# Revit family: Ворота ВПО-60
name_source: partatom
category: Двери
revit_build: Autodesk Revit 2017 (Build: 20160225_1515(x64)
units: mm (PartAtom-declared; Revit-internal decimal feet)

## family parameters
Всегда вертикально = Да
Заголовок OmniClass = Doors
Номер OmniClass = 23.30.10.00
Общий = Нет
Основа = Стена
При загрузке вырезать с полостями = Нет
Точка расчета площади = Нет

## types (10) — shared parameters
ADSK_URL страницы изделия = http://dwrcenter.ru
ADSK_Завод-изготовитель = ДВР Центр, г.Москва
ADSK_Наименование = ВПО-ОГНЕДЕКОР-60К
ADSK_Наименование краткое = ВПО-60
ADSK_Обозначение = ГОСТ 31174-2003, ГОСТ 53307-2009
ADSK_Предел огнестойкости = EI-60
URL = http://dwrcenter.ru
Группа модели = Ворота
Замыкание стены = По основе
Изготовитель = ДВР Центр, г.Москва, +7-495-4-112-911
Материал коробки = <По категории>
Материал створки = <По категории>
Огнестойкость = EI-60
Описание = Ворота противопожарные откатные
Телефоны изготовителя = +7-495-4-112-911, +7-495-5-103-206
Тип конструкций = Ворота противопожарные откатные, ГОСТ 53307-2009
Толщина = 260 мм
Функция = Внутренние слои
zero-valued in all types: ADSK_Количество, ADSK_Откосы_Глубина, ADSK_Толщина стены, ADSK_Толщина стены (отчет)

## per-type parameters (varying)
| type | ADSK_Открывание | Вылет на плане | Высота | До привода | Левое исполнение | Правое исполнение | Привод | Противовес | Сдвиг балки влево | Сдвиг балки вправо | Смещение противовеса | Смещение ручки | Ширина | Ширина секции | Ширина створки | Электромеханический привод |
| ВПО-ОГНЕДЕКОР-60Кп, проем 3000х3000 | Правое исполнение | 1248 мм | 3000 мм | 2820 мм | Нет | Да | Алюминий | Нет | 0 мм | 3120 мм | 3340 мм | 2902 мм | 3000 мм | 624 мм | 3120 мм | Нет |
| ВПО-ОГНЕДЕКОР-60Кл, проем 3000х3000 | Левое исполнение | 1248 мм | 3000 мм | 100 мм | Да | Нет | <По категории> | Да | 3120 мм | 0 мм | 0 мм | 109 мм | 3000 мм | 624 мм | 3120 мм | Да |
| ВПО-ОГНЕДЕКОР-60Кп, проем 3000х2500 | Правое исполнение | 1248 мм | 2500 мм | 2820 мм | Нет | Да | <По категории> | Да | 0 мм | 3120 мм | 3340 мм | 2902 мм | 3000 мм | 624 мм | 3120 мм | Да |
| ВПО-ОГНЕДЕКОР-60Кл, проем 3000х2500 | Левое исполнение | 1248 мм | 2500 мм | 100 мм | Да | Нет | <По категории> | Да | 3120 мм | 0 мм | 0 мм | 109 мм | 3000 мм | 624 мм | 3120 мм | Да |
| ВПО-ОГНЕДЕКОР-60Кп, проем 3500х2500 | Правое исполнение | 1448 мм | 2500 мм | 3320 мм | Нет | Да | <По категории> | Да | 0 мм | 3620 мм | 3840 мм | 3402 мм | 3500 мм | 724 мм | 3620 мм | Да |
| ВПО-ОГНЕДЕКОР-60Кл, проем 3500х2500 | Левое исполнение | 1448 мм | 2500 мм | 100 мм | Да | Нет | <По категории> | Да | 3620 мм | 0 мм | 0 мм | 109 мм | 3500 мм | 724 мм | 3620 мм | Да |
| ВПО-ОГНЕДЕКОР-60Кп, проем 3500х3000 | Правое исполнение | 1448 мм | 3000 мм | 3320 мм | Нет | Да | <По категории> | Да | 0 мм | 3620 мм | 3840 мм | 3402 мм | 3500 мм | 724 мм | 3620 мм | Да |
| ВПО-ОГНЕДЕКОР-60Кл, проем 3500х3000 | Левое исполнение | 1448 мм | 3000 мм | 100 мм | Да | Нет | <По категории> | Да | 3620 мм | 0 мм | 0 мм | 109 мм | 3500 мм | 724 мм | 3620 мм | Да |
| ВПО-ОГНЕДЕКОР-60Кп, проем 2500х2500 | Правое исполнение | 1048 мм | 2500 мм | 2320 мм | Нет | Да | <По категории> | Да | 0 мм | 2620 мм | 2840 мм | 2402 мм | 2500 мм | 524 мм | 2620 мм | Да |
| ВПО-ОГНЕДЕКОР-60Кл, проем 2500х2500 | Левое исполнение | 1048 мм | 2500 мм | 100 мм | Да | Нет | <По категории> | Да | 2620 мм | 0 мм | 0 мм | 109 мм | 2500 мм | 524 мм | 2620 мм | Да |
